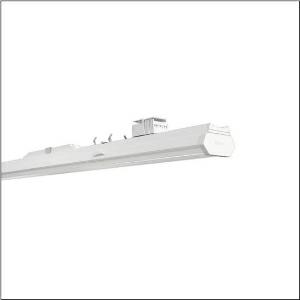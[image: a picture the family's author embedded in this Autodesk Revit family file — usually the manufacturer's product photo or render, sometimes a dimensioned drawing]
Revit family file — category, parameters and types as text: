
# Revit family: licross_r__11_protected_mo_51tp11dn49xfd_8d42
name_source: partatom
category: Lighting Fixtures
units: mm (PartAtom-declared; Revit-internal decimal feet)

## family parameters
Cut with Voids When Loaded = No
Host = Face
Light Source = No
Part Type = Normal
Room Calculation Point = No
Round Connector Dimension = Use Diameter
Shared = No

## types (1)
- --- (1 x LED, 1440 lm, 10.2 W, 4000K)
    Apparent Load = 10 VA
    CIE Flux Codes = 83 94 98 100 100
    Color Rendering = 80
    Color Temperature = 4000K
    Default Elevation = 1800 mm
    Description = Licross® 11 Protected MOluminaire insert, length: 1.500mm, width: 90mm, height: 101mm, LED rated luminous flux: 9.080lm, light colour: 840, control gear: DALI 2, control gear: ECG DALI, with plug, 6-pole, with phase selection, mains connection: 220..240V, AC/DC, 0/50..60Hz, without changeover relay, for emergency light function, for central battery installations according to DIN EN 60598-2-22, halogen-free wiring, primary optical cover: cover, of PMMA, light emission: direct with ceiling illumination distribution, protection rating (complete): IP64, insulation class (complete): insulation class I (protective earthing), certification: CE, ENEC, VDE, protection symbol: D if used in an environment without relevant dust loads with corresponding accessories, permissible ambient temperature for indoor applications: -25..+40°C, standard: EN 60598-2-22, reducing of maximum allowable ambient temperature of 5°C with ceiling mounting, corresponds to IFS (International Featured Standards) requirements for safety and quality in the food industry, packaging unit: 1 piece
    Height = 92 mm
    Lamp = 1 x LED
    Lamp Light Flux = 1440 lm
    Lamp Power = 10.2 W
    Lamp count = 1
    Length = 1500 mm
    Luminous efficacy = 141 lm/W
    Manufacturer = Siteco
    ModVariant = No
    Model = 51TP11DN49XFD
    Mounting Place = Ceiling
    Mounting Type = Pendant
    Number of Poles = 1
    OnlyDefault = Yes
    Power Factor = 1
    Product Name = Licross® 11 Protected MO
    Product group = luminaire insert
    ProductGroupID = 902
    Protection Class = Protection class I
    Protection Degree = IP 64
    RLX_Detail_Level = 1
    RlxData = <blob elided: 24109 chars, md5=a9427e14>
    Socket = socket
    Standby Power = 0 W
    System Light Flux = 1440 lm
    System Power = 10 W
    Type Comments = : DC mode (central or group accumulator) initial emergency light level
    Type Image = l_1256148.jpg
    URL = http://relux.com
    VarID = @adj_134589
    Voltage = 0 V
    Weight = 0.00 kg
    Width = 88 mm

## geometry (parser evidence)
native form markers: Blend x4, Sweep x10
no freeform markers — native parametric forms only
